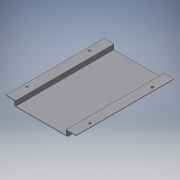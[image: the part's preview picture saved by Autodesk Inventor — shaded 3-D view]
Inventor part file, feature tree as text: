
AUTODESK INVENTOR PART (.ipt)
format: ipt  version: 2016 SP2 (Build 200236200, 236)  size: 125,952 bytes
history: native  units: mm
features: reference x6, extrude x3, sketch x2, projected_geometry x1
ambient origin geometry x8: Origin, YZ Plane, XZ Plane, XY Plane, X Axis, Y Axis, Z Axis, Center Point
bodies: Volumenkörper1 (feature_tree)
feature tree (12):
  extrude  "Extrusion1"  Depth=12.0mm
  extrude  "Extrusion3"  Depth=7.0mm TaperAngle=0.0deg
  extrude  "Extrusion4"  Depth=2.0mm
  sketch  "Skizze2"  dims[d2=0.6mm d3=0.0mm d4=12.0mm]
  sketch  "Skizze3"  dims[d5=12.0mm d8=7.0mm d9=0.0mm d10=2.0mm d11=2.0mm d12=7.0mm d13=0.0mm d14=25.75mm d15=25.0mm]
  projected_geometry  "Projizierte Kontur1"
  reference  "Referenz9"
  reference  "Referenz10"
  reference  "Referenz11"
  reference  "Referenz12"
  reference  "Referenz13"
  reference  "Referenz14"
